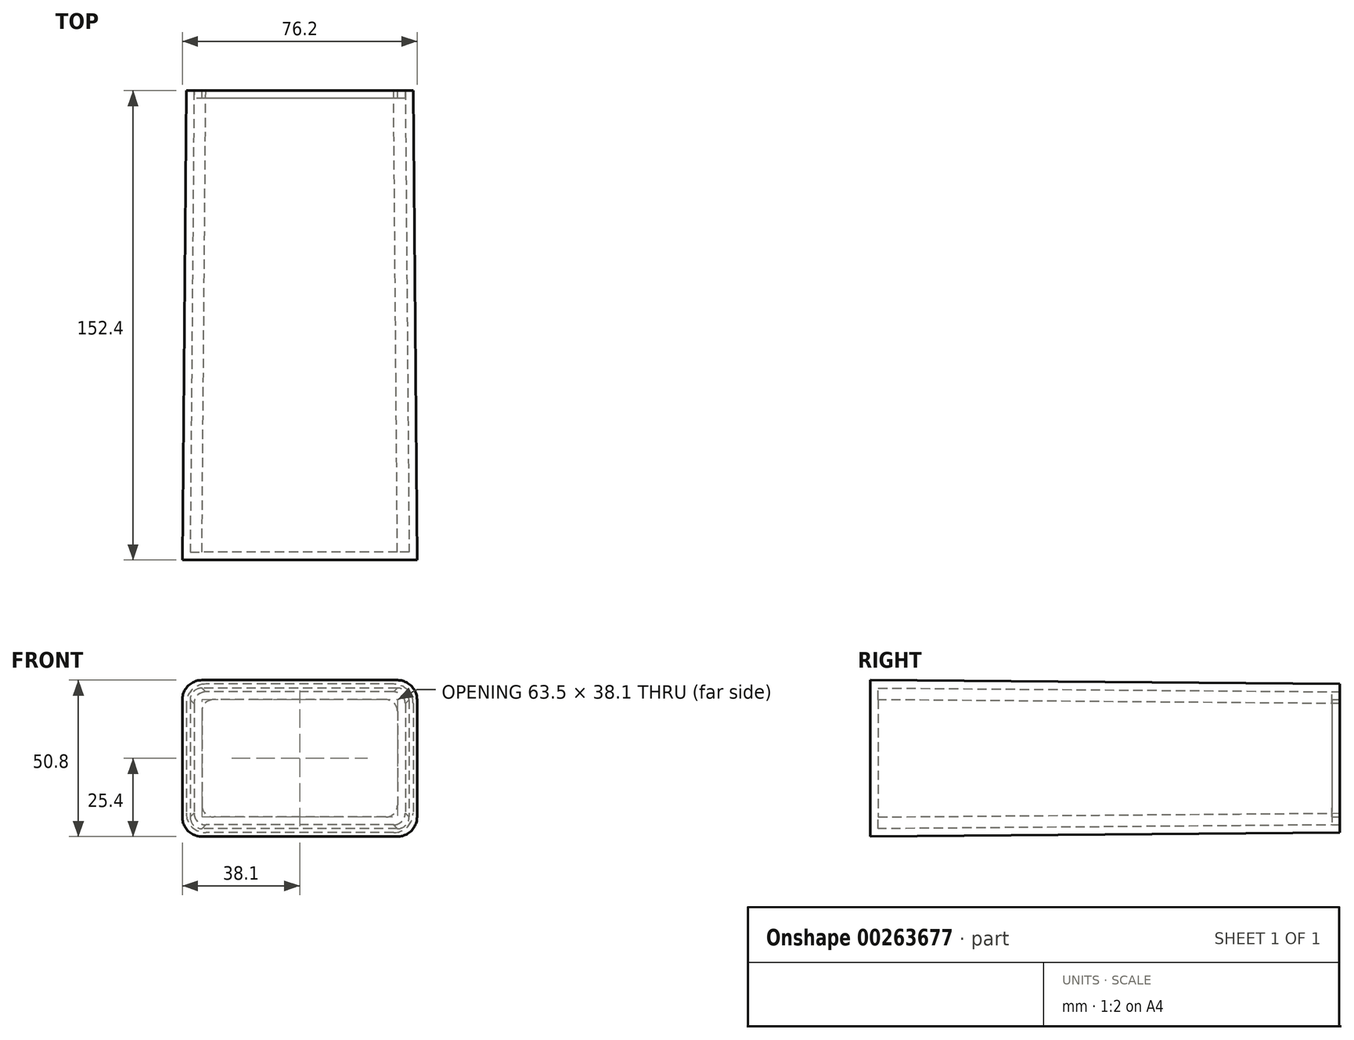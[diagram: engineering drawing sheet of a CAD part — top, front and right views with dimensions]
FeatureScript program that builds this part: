
annotation { "Feature Type Name" : "Feature", "Feature Type Description" : "" }
export const myFeature = defineFeature(function(context is Context, id is Id, definition is map)
    precondition{}
    {
        {
            var Q0;
            Q0=qCreatedBy(makeId("Front.planeOp"),FACE);
            cPlane(context, id + "F0", {"entities" : qUnion([Q0]), "cplaneType" : CPlaneType.OFFSET, "offset" : 152.4 * mm, "oppositeDirection" : true, "width" : 152.4 * mm, "height" : 152.4 * mm});
        }
        {
            var Q0;
            Q0=qCreatedBy(makeId("Front.planeOp"),FACE);
            var sketch = newSketch(context, id + "F1", { "sketchPlane" : qUnion([Q0])});
            skLineSegment(sketch, "E0.bottom", {"start": v(-69.85, 50.8) * mm, "end": v(-6.35, 50.8) * mm});
            skLineSegment(sketch, "E0.top", {"start": v(-69.85, 0) * mm, "end": v(-6.35, 0) * mm});
            skLineSegment(sketch, "E0.left", {"start": v(-76.2, 44.45) * mm, "end": v(-76.2, 6.35) * mm});
            skLineSegment(sketch, "E0.right", {"start": v(0, 44.45) * mm, "end": v(0, 6.35) * mm});
            skPoint(sketch, "E1.visualSharp", {"position": v(0, 50.8) * mm});
            skArc(sketch, "E1.filletArc", {"start": v(0, 44.45) * mm, "mid": v(-1.86, 48.94) * mm, "end": v(-6.35, 50.8) * mm});
            skPoint(sketch, "E2.visualSharp", {"position": v(0, 0) * mm});
            skArc(sketch, "E2.filletArc", {"start": v(-6.35, 0) * mm, "mid": v(-1.86, 1.86) * mm, "end": v(0, 6.35) * mm});
            skPoint(sketch, "E3.visualSharp", {"position": v(-76.2, 0) * mm});
            skArc(sketch, "E3.filletArc", {"start": v(-76.2, 6.35) * mm, "mid": v(-74.34, 1.86) * mm, "end": v(-69.85, 0) * mm});
            skPoint(sketch, "E4.visualSharp", {"position": v(-76.2, 50.8) * mm});
            skArc(sketch, "E4.filletArc", {"start": v(-69.85, 50.8) * mm, "mid": v(-74.34, 48.94) * mm, "end": v(-76.2, 44.45) * mm});
            skSolve(sketch);
        }
        {
            var Q0;
            Q0=qCreatedBy(id+"F0.planeOp",FACE);
            var sketch = newSketch(context, id + "F2", { "sketchPlane" : qUnion([Q0])});
            skLineSegment(sketch, "E5.bottom", {"start": v(-7.62, 49.53) * mm, "end": v(-68.58, 49.53) * mm});
            skLineSegment(sketch, "E5.top", {"start": v(-7.62, 1.27) * mm, "end": v(-68.58, 1.27) * mm});
            skLineSegment(sketch, "E5.left", {"start": v(-1.27, 43.18) * mm, "end": v(-1.27, 7.62) * mm});
            skLineSegment(sketch, "E5.right", {"start": v(-74.93, 43.18) * mm, "end": v(-74.93, 7.62) * mm});
            skPoint(sketch, "E5.middle", {"position": v(-38.1, 25.4) * mm});
            skPoint(sketch, "E6.visualSharp", {"position": v(-1.27, 49.53) * mm});
            skArc(sketch, "E6.filletArc", {"start": v(-1.27, 43.18) * mm, "mid": v(-3.13, 47.67) * mm, "end": v(-7.62, 49.53) * mm});
            skPoint(sketch, "E7.visualSharp", {"position": v(-74.93, 49.53) * mm});
            skArc(sketch, "E7.filletArc", {"start": v(-68.58, 49.53) * mm, "mid": v(-73.07, 47.67) * mm, "end": v(-74.93, 43.18) * mm});
            skPoint(sketch, "E8.visualSharp", {"position": v(-74.93, 1.27) * mm});
            skArc(sketch, "E8.filletArc", {"start": v(-74.93, 7.62) * mm, "mid": v(-73.07, 3.13) * mm, "end": v(-68.58, 1.27) * mm});
            skPoint(sketch, "E9.visualSharp", {"position": v(-1.27, 1.27) * mm});
            skArc(sketch, "E9.filletArc", {"start": v(-7.62, 1.27) * mm, "mid": v(-3.13, 3.13) * mm, "end": v(-1.27, 7.62) * mm});
            skLineSegment(sketch, "E10.bottom", {"start": v(-68.58, 49.53) * mm, "end": v(-7.62, 49.53) * mm});
            skLineSegment(sketch, "E11.left", {"start": v(-74.93, 7.62) * mm, "end": v(-74.93, 43.18) * mm});
            skSolve(sketch);
        }
        {
            var Q0;
            Q0=makeQuery(id+"F2.imprint","IMPRINT",FACE,{"disambiguationData":[TD([[makeQuery(id+"F2.imprint","IMPRINT",EDGE,{"derivedFrom":sQuery(id+"F2.wireOp",EDGE,"E6.filletArc")}),1.0]])]});
            var Q1;
            Q1=makeQuery(id+"F1.imprint","IMPRINT",FACE,{"disambiguationData":[TD([[makeQuery(id+"F1.imprint","IMPRINT",EDGE,{"derivedFrom":sQuery(id+"F1.wireOp",EDGE,"E0.bottom")}),-1.0]])]});
            loft(context, id + "F3", {"sheetProfilesArray" : [{ "sheetProfileEntities" : qUnion([Q0]) }, { "sheetProfileEntities" : qUnion([Q1]) }]});
        }
        {
            var Q0;
            Q0=makeQuery(id+"F3.opLoft","CAP_FACE",FACE,{"disambiguationData":[OSD([makeQuery(id+"F2.imprint","IMPRINT",FACE,{"disambiguationData":[TD([[makeQuery(id+"F2.imprint","IMPRINT",EDGE,{"derivedFrom":sQuery(id+"F2.wireOp",EDGE,"E6.filletArc")}),1.0]])]})])],"isStart":true});
            shell(context, id + "F4", {"entities" : qUnion([Q0]), "thickness" : 2.54 * mm});
        }
        {
            var Q0;
            Q0=qCreatedBy(id+"F0.planeOp",FACE);
            var sketch = newSketch(context, id + "F5", { "sketchPlane" : qUnion([Q0])});
            skLineSegment(sketch, "E12.bottom", {"start": v(-7.62, 46.99) * mm, "end": v(-68.58, 46.99) * mm});
            skLineSegment(sketch, "E12.top", {"start": v(-7.62, 3.81) * mm, "end": v(-68.58, 3.81) * mm});
            skLineSegment(sketch, "E12.left", {"start": v(-3.81, 43.18) * mm, "end": v(-3.81, 7.62) * mm});
            skLineSegment(sketch, "E12.right", {"start": v(-72.39, 43.18) * mm, "end": v(-72.39, 7.62) * mm});
            skLineSegment(sketch, "E13.bottom", {"start": v(-10.16, 44.45) * mm, "end": v(-66.04, 44.45) * mm});
            skLineSegment(sketch, "E13.top", {"start": v(-10.16, 6.35) * mm, "end": v(-66.04, 6.35) * mm});
            skLineSegment(sketch, "E13.left", {"start": v(-6.35, 40.64) * mm, "end": v(-6.35, 10.16) * mm});
            skLineSegment(sketch, "E13.right", {"start": v(-69.85, 40.64) * mm, "end": v(-69.85, 10.16) * mm});
            skPoint(sketch, "E14.visualSharp", {"position": v(-3.81, 3.81) * mm});
            skArc(sketch, "E14.filletArc", {"start": v(-7.62, 3.81) * mm, "mid": v(-4.93, 4.93) * mm, "end": v(-3.81, 7.62) * mm});
            skPoint(sketch, "E15.visualSharp", {"position": v(-3.81, 46.99) * mm});
            skArc(sketch, "E15.filletArc", {"start": v(-3.81, 43.18) * mm, "mid": v(-4.93, 45.87) * mm, "end": v(-7.62, 46.99) * mm});
            skPoint(sketch, "E16.visualSharp", {"position": v(-72.39, 46.99) * mm});
            skArc(sketch, "E16.filletArc", {"start": v(-68.58, 46.99) * mm, "mid": v(-71.27, 45.87) * mm, "end": v(-72.39, 43.18) * mm});
            skPoint(sketch, "E17.visualSharp", {"position": v(-72.39, 3.81) * mm});
            skArc(sketch, "E17.filletArc", {"start": v(-72.39, 7.62) * mm, "mid": v(-71.27, 4.93) * mm, "end": v(-68.58, 3.81) * mm});
            skPoint(sketch, "E18.visualSharp", {"position": v(-69.85, 6.35) * mm});
            skArc(sketch, "E18.filletArc", {"start": v(-69.85, 10.16) * mm, "mid": v(-68.73, 7.47) * mm, "end": v(-66.04, 6.35) * mm});
            skPoint(sketch, "E19.visualSharp", {"position": v(-69.85, 44.45) * mm});
            skArc(sketch, "E19.filletArc", {"start": v(-66.04, 44.45) * mm, "mid": v(-68.73, 43.33) * mm, "end": v(-69.85, 40.64) * mm});
            skPoint(sketch, "E20.visualSharp", {"position": v(-6.35, 44.45) * mm});
            skArc(sketch, "E20.filletArc", {"start": v(-6.35, 40.64) * mm, "mid": v(-7.47, 43.33) * mm, "end": v(-10.16, 44.45) * mm});
            skPoint(sketch, "E21.visualSharp", {"position": v(-6.35, 6.35) * mm});
            skArc(sketch, "E21.filletArc", {"start": v(-10.16, 6.35) * mm, "mid": v(-7.47, 7.47) * mm, "end": v(-6.35, 10.16) * mm});
            skSolve(sketch);
        }
        {
            var Q0;
            Q0=makeQuery(id+"F5.imprint","IMPRINT",FACE,{"disambiguationData":[TD([[makeQuery(id+"F5.imprint","IMPRINT",EDGE,{"derivedFrom":sQuery(id+"F5.wireOp",EDGE,"E12.bottom")}),1.0]])]});
            extrude(context, id + "F6", {"entities" : qUnion([Q0]), "depth" : 2.54 * mm});
        }
    });
